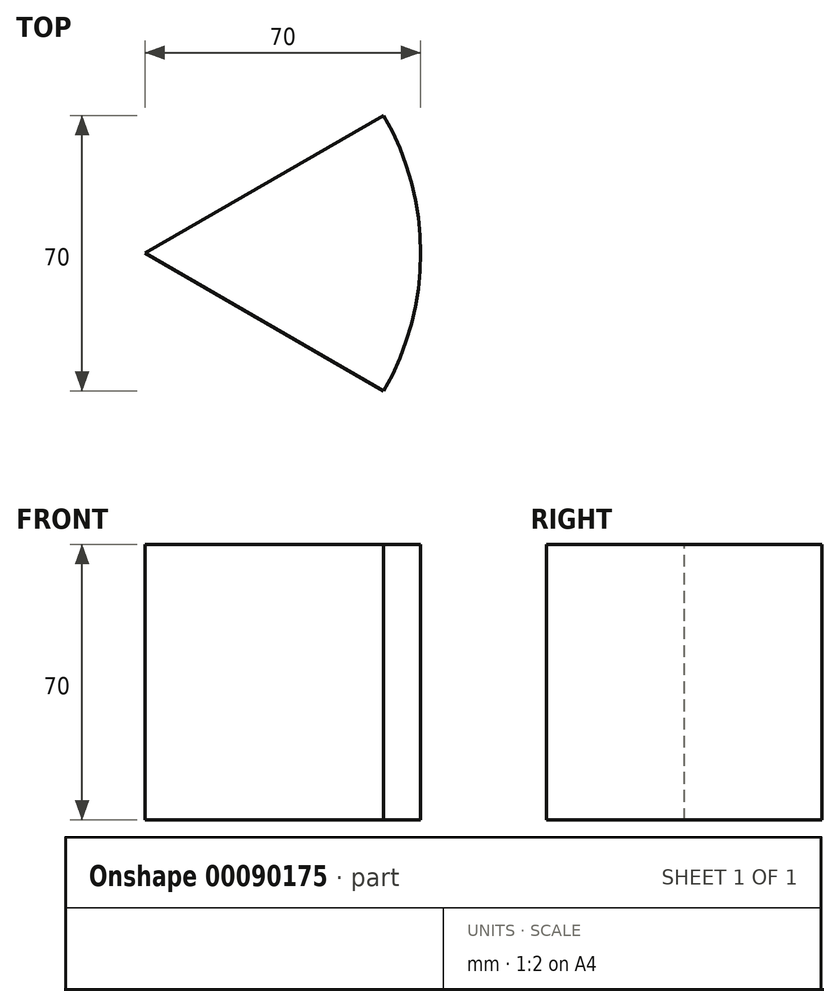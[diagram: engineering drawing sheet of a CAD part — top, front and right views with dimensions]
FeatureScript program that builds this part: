
annotation { "Feature Type Name" : "Feature", "Feature Type Description" : "" }
export const myFeature = defineFeature(function(context is Context, id is Id, definition is map)
    precondition{}
    {
        {
            var Q0;
            Q0=qCreatedBy(makeId("Front.planeOp"),FACE);
            var sketch = newSketch(context, id + "F0", { "sketchPlane" : qUnion([Q0])});
            skLineSegment(sketch, "E0.bottom", {"start": v(0, 0) * mm, "end": v(70, 0) * mm});
            skLineSegment(sketch, "E0.top", {"start": v(0, 70) * mm, "end": v(70, 70) * mm});
            skLineSegment(sketch, "E0.left", {"start": v(0, 0) * mm, "end": v(0, 70) * mm});
            skLineSegment(sketch, "E0.right", {"start": v(70, 0) * mm, "end": v(70, 70) * mm});
            skSolve(sketch);
        }
        {
            var Q0;
            Q0=makeQuery(id+"F0.imprint","IMPRINT",FACE,{"disambiguationData":[TD([[makeQuery(id+"F0.imprint","IMPRINT",EDGE,{"derivedFrom":sQuery(id+"F0.wireOp",EDGE,"E0.bottom")}),1.0]])]});
            var Q1;
            Q1=sQuery(id+"F0.wireOp",EDGE,"E0.left");
            revolve(context, id + "F1", {"entities" : qUnion([Q0]), "axis" : qUnion([Q1]), "revolveType" : RevolveType.SYMMETRIC, "angle" : 60 * degree});
        }
    });
